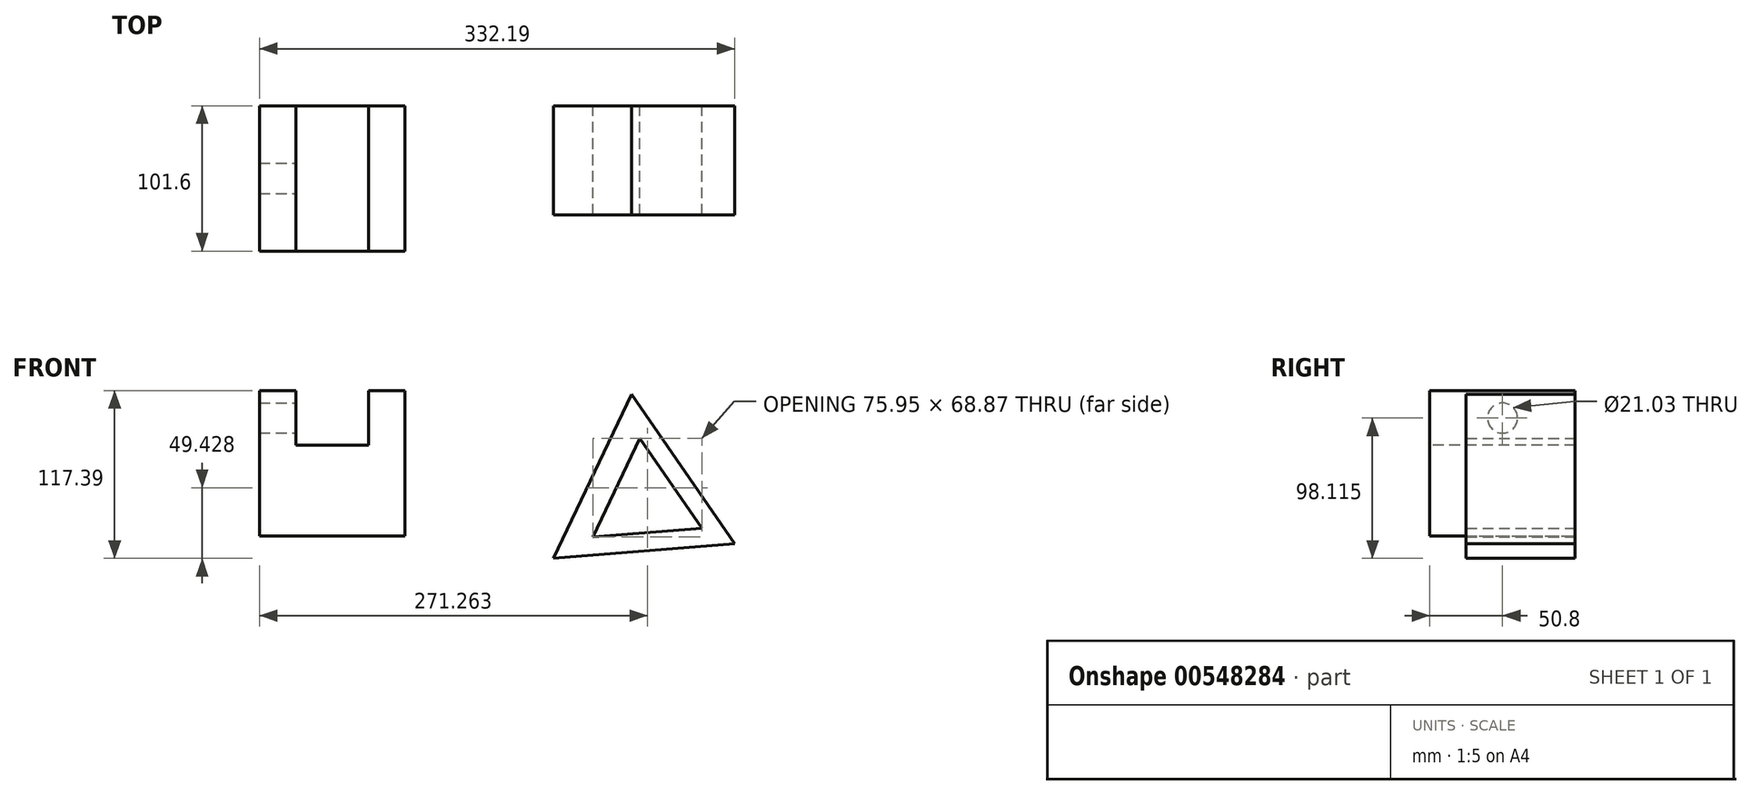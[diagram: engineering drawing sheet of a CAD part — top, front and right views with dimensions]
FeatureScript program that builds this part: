
annotation { "Feature Type Name" : "Feature", "Feature Type Description" : "" }
export const myFeature = defineFeature(function(context is Context, id is Id, definition is map)
    precondition{}
    {
        {
            var Q0;
            Q0=qCreatedBy(makeId("Front.planeOp"),FACE);
            var sketch = newSketch(context, id + "F0", { "sketchPlane" : qUnion([Q0])});
            skLineSegment(sketch, "E0.bottom", {"start": v(-96.67, 15.8) * mm, "end": v(4.93, 15.8) * mm});
            skLineSegment(sketch, "E0.top", {"start": v(-96.67, 117.4) * mm, "end": v(4.93, 117.4) * mm});
            skLineSegment(sketch, "E0.left", {"start": v(-96.67, 15.8) * mm, "end": v(-96.67, 117.4) * mm});
            skLineSegment(sketch, "E0.right", {"start": v(4.93, 15.8) * mm, "end": v(4.93, 117.4) * mm});
            skSolve(sketch);
        }
        {
            var Q0;
            Q0=makeQuery(id+"F0.imprint","IMPRINT",FACE,{"disambiguationData":[TD([[makeQuery(id+"F0.imprint","IMPRINT",EDGE,{"derivedFrom":sQuery(id+"F0.wireOp",EDGE,"E0.bottom")}),1.0]])]});
            extrude(context, id + "F1", {"entities" : qUnion([Q0]), "depth" : 101.6 * mm, "offsetDistance" : 25.4 * mm});
        }
        {
            var Q0;
            Q0=makeQuery(id+"F1.opExtrude","CAP_FACE",FACE,{"disambiguationData":[OSD([sQuery(id+"F0.wireOp",EDGE,"E0.bottom"),sQuery(id+"F0.wireOp",EDGE,"E0.top"),sQuery(id+"F0.wireOp",EDGE,"E0.left"),sQuery(id+"F0.wireOp",EDGE,"E0.right")])],"isStart":false});
            var sketch = newSketch(context, id + "F2", { "sketchPlane" : qUnion([Q0])});
            skLineSegment(sketch, "E1", {"start": v(-96.67, 101.12) * mm, "end": v(-71.27, 101.12) * mm});
            skLineSegment(sketch, "E2", {"start": v(-71.27, 101.12) * mm, "end": v(-71.27, 79.3) * mm});
            skLineSegment(sketch, "E3", {"start": v(-71.27, 79.3) * mm, "end": v(-20.47, 79.3) * mm});
            skLineSegment(sketch, "E4", {"start": v(-20.47, 79.3) * mm, "end": v(-20.47, 101.12) * mm});
            skLineSegment(sketch, "E5", {"start": v(-20.47, 101.12) * mm, "end": v(4.93, 101.12) * mm});
            skLineSegment(sketch, "E6", {"start": v(-71.27, 101.12) * mm, "end": v(-71.27, 117.4) * mm});
            skLineSegment(sketch, "E7", {"start": v(-71.27, 117.4) * mm, "end": v(-20.47, 117.4) * mm});
            skLineSegment(sketch, "E8", {"start": v(-20.47, 117.4) * mm, "end": v(-20.47, 101.12) * mm});
            skSolve(sketch);
        }
        {
            var Q0;
            Q0=makeQuery(id+"F2.imprint","IMPRINT",FACE,{"disambiguationData":[TD([[makeQuery(id+"F2.imprint","IMPRINT",EDGE,{"derivedFrom":sQuery(id+"F2.wireOp",EDGE,"E2")}),1.0]])]});
            extrude(context, id + "F3", {"entities" : qUnion([Q0]), "operationType" : NewBodyOperationType.REMOVE, "oppositeDirection" : true, "depth" : 130.8 * mm, "offsetDistance" : 25.4 * mm});
        }
        {
            var Q0;
            Q0=makeQuery(id+"F3.boolean.opBoolean","COPY",FACE,{"derivedFrom":makeQuery(id+"F3.opExtrude","SWEPT_FACE",FACE,{"disambiguationData":[OSD([sQuery(id+"F2.wireOp",EDGE,"E2"),sQuery(id+"F2.wireOp",EDGE,"E6")])]})});
            var sketch = newSketch(context, id + "F4", { "sketchPlane" : qUnion([Q0])});
            skCircle(sketch, "E9", {"center": v(-50.8, 98.11) * mm, "radius": 10.51 * mm});
            skPoint(sketch, "E9.centerSnap0", {"position": v(-50.8, 117.4) * mm});
            skSolve(sketch);
        }
        {
            var Q0;
            Q0=makeQuery(id+"F4.imprint","IMPRINT",FACE,{"disambiguationData":[TD([[makeQuery(id+"F4.imprint","IMPRINT",EDGE,{"derivedFrom":sQuery(id+"F4.wireOp",EDGE,"E9")}),1.0]])]});
            extrude(context, id + "F5", {"entities" : qUnion([Q0]), "operationType" : NewBodyOperationType.REMOVE, "oppositeDirection" : true, "depth" : 25.4 * mm, "offsetDistance" : 25.4 * mm});
        }
        {
            var Q0;
            Q0=qCreatedBy(makeId("Front.planeOp"),FACE);
            var sketch = newSketch(context, id + "F6", { "sketchPlane" : qUnion([Q0])});
            skLineSegment(sketch, "E10", {"start": v(163.3, 114.78) * mm, "end": v(235.52, 10.3) * mm});
            skLineSegment(sketch, "E11", {"start": v(235.52, 10.3) * mm, "end": v(108.94, 0) * mm});
            skLineSegment(sketch, "E12", {"start": v(108.94, 0) * mm, "end": v(163.3, 114.78) * mm});
            skSolve(sketch);
        }
        {
            var Q0;
            Q0=makeQuery(id+"F6.imprint","IMPRINT",FACE,{"disambiguationData":[TD([[makeQuery(id+"F6.imprint","IMPRINT",EDGE,{"derivedFrom":sQuery(id+"F6.wireOp",EDGE,"E10")}),-1.0]])]});
            extrude(context, id + "F7", {"entities" : qUnion([Q0]), "depth" : 76.2 * mm, "offsetDistance" : 25.4 * mm});
        }
        {
            var Q0;
            Q0=makeQuery(id+"F7.opExtrude","CAP_FACE",FACE,{"disambiguationData":[OSD([sQuery(id+"F6.wireOp",EDGE,"E10"),sQuery(id+"F6.wireOp",EDGE,"E11"),sQuery(id+"F6.wireOp",EDGE,"E12")])],"isStart":true});
            var sketch = newSketch(context, id + "F8", { "sketchPlane" : qUnion([Q0])});
            skLineSegment(sketch, "E13", {"start": v(-169.24, 83.86) * mm, "end": v(-212.57, 21.18) * mm});
            skLineSegment(sketch, "E14", {"start": v(-212.57, 21.18) * mm, "end": v(-136.62, 15) * mm});
            skLineSegment(sketch, "E15", {"start": v(-169.24, 83.86) * mm, "end": v(-136.62, 15) * mm});
            skSolve(sketch);
        }
        {
            var Q0;
            Q0=makeQuery(id+"F8.imprint","IMPRINT",FACE,{"disambiguationData":[TD([[makeQuery(id+"F8.imprint","IMPRINT",EDGE,{"derivedFrom":sQuery(id+"F8.wireOp",EDGE,"E13")}),1.0]])]});
            extrude(context, id + "F9", {"entities" : qUnion([Q0]), "operationType" : NewBodyOperationType.REMOVE, "oppositeDirection" : true, "depth" : 76.2 * mm, "offsetDistance" : 25.4 * mm});
        }
    });
